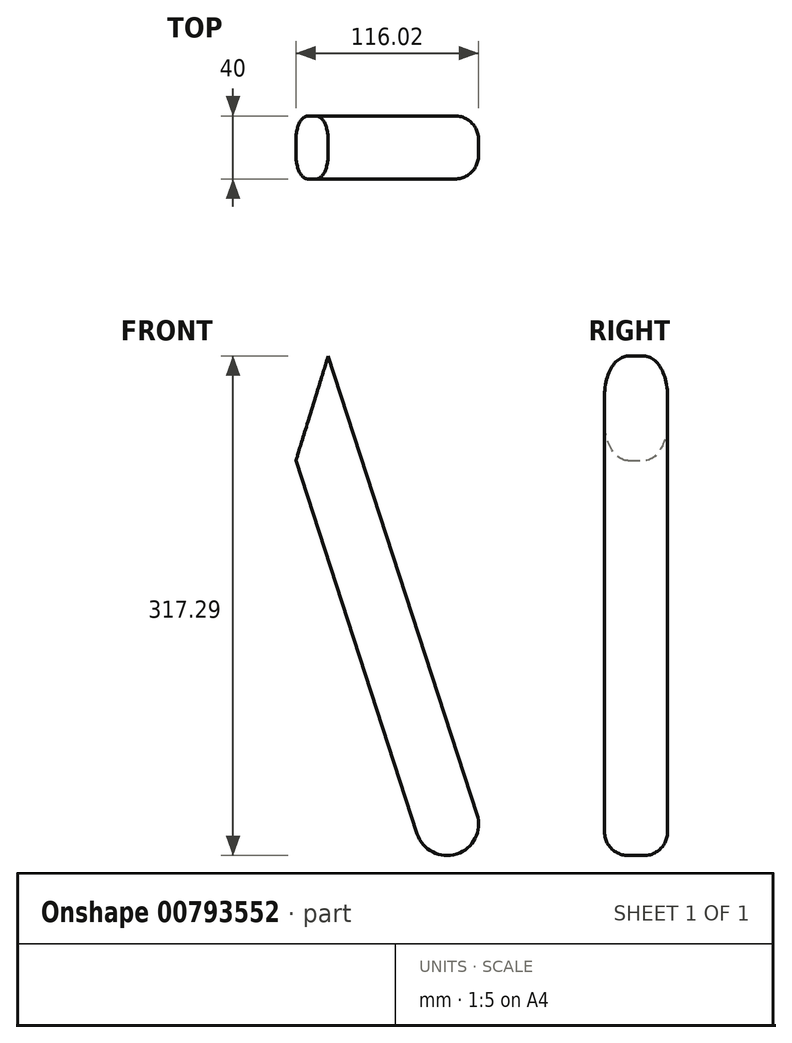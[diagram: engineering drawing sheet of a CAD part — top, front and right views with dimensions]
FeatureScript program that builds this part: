
annotation { "Feature Type Name" : "Feature", "Feature Type Description" : "" }
export const myFeature = defineFeature(function(context is Context, id is Id, definition is map)
    precondition{}
    {
        {
            var Q0;
            Q0=qCreatedBy(makeId("Front.planeOp"),FACE);
            var sketch = newSketch(context, id + "F0", { "sketchPlane" : qUnion([Q0])});
            skLineSegment(sketch, "E0", {"start": v(0, 0) * mm, "end": v(0, 650) * mm, "construction": true});
            skLineSegment(sketch, "E1", {"start": v(0, 650) * mm, "end": v(-300, 650) * mm, "construction": true});
            skLineSegment(sketch, "E2", {"start": v(0, 0) * mm, "end": v(-250, 0) * mm, "construction": true});
            skLineSegment(sketch, "E3", {"start": v(-162.95, 282.9) * mm, "end": v(-50, 650) * mm, "construction": true});
            skLineSegment(sketch, "E4", {"start": v(0, 0) * mm, "end": v(-50, 0) * mm, "construction": true});
            skLineSegment(sketch, "E5.0", {"start": v(-30.98, 6.18) * mm, "end": v(-133.7, 322.33) * mm});
            skLineSegment(sketch, "E6.0", {"start": v(-69.02, -6.18) * mm, "end": v(-152.2, 249.83) * mm});
            skLineSegment(sketch, "E7.0", {"start": v(-230.88, -5.88) * mm, "end": v(-229.07, 0) * mm});
            skLineSegment(sketch, "E8.trimOffspring", {"start": v(-152.2, 249.83) * mm, "end": v(-131.75, 316.31) * mm});
            skLineSegment(sketch, "E9", {"start": v(-50, 0) * mm, "end": v(-56.18, 19.02) * mm, "construction": true});
            skArc(sketch, "E10", {"start": v(-75.2, 12.84) * mm, "mid": v(-50, 0) * mm, "end": v(-37.16, 25.2) * mm});
            skSolve(sketch);
        }
        {
            var Q0;
            Q0 = qSketchRegion(id + "F0", true);
            extrude(context, id + "F1", {"entities" : qUnion([Q0]), "depth" : 40 * mm, "offsetDistance" : 25 * mm});
        }
        {
            var Q0;
            Q0=makeQuery(id+"F1.opExtrude","CAP_EDGE",EDGE,{"disambiguationData":[OSD([sQuery(id+"F0.wireOp",EDGE,"E6.0")])],"isStart":true});
            var Q1;
            Q1=makeQuery(id+"F1.opExtrude","CAP_EDGE",EDGE,{"disambiguationData":[OSD([sQuery(id+"F0.wireOp",EDGE,"E5.0")])],"isStart":true});
            var Q2;
            Q2=makeQuery(id+"F1.opExtrude","CAP_EDGE",EDGE,{"disambiguationData":[OSD([sQuery(id+"F0.wireOp",EDGE,"E6.0")])],"isStart":false});
            var Q3;
            Q3=makeQuery(id+"F1.opExtrude","CAP_EDGE",EDGE,{"disambiguationData":[OSD([sQuery(id+"F0.wireOp",EDGE,"E5.0")])],"isStart":false});
            fillet(context, id + "F2", {"entities" : qUnion([Q0, Q1, Q2, Q3]), "radius" : 15 * mm, "tangentPropagation" : true, "allowEdgeOverflow" : false});
        }
    });
